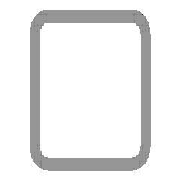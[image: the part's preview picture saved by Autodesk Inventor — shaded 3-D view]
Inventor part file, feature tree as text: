
AUTODESK INVENTOR PART (.ipt)
format: ipt  version: 2017 (Build 210142000, 142)  size: 133,120 bytes
history: native  units: mm (DEFAULTED — no unit token found)
features: other x4, plane x3, sketch x3, split x2
ambient origin geometry x8: Origin, YZ Plane, XZ Plane, XY Plane, X Axis, Y Axis, Z Axis, Center Point
bodies: Solid1 (feature_tree), Body (feature_tree)
feature tree (12):
  parser-record x1  (decoder bookkeeping rows leaked as tree rows — omitted from the tree; the rows remain in map.json)
  other  "Driven Length"
  other  "Start plane"
  other  "End plane"
  plane  "Work Plane4"
  split  "Split1"
  plane  "Work Plane5"
  split  "Split2"
  sketch  "Sketch"  dims[d10=76.2mm d11=76.2mm d12=6.35mm d13=266.7mm d14=952.5mm d15=38.1mm d16=38.1mm d17=12.7mm d18=90.0deg d19=685.8mm]
  sketch  "Sketch3"  dims[d3=685.8mm]
  plane  "Work Plane3"
  sketch  "Sketch4"  dims[d4=0.0mm]
